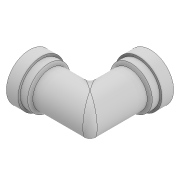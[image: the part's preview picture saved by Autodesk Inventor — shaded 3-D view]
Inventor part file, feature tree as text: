
AUTODESK INVENTOR PART (.ipt)
format: ipt  version: 2021 (Build 250183000, 183)  size: 292,864 bytes
history: native  units: mm
features: other x4, sketch x2, revolve x1, mirror x1, fillet x1
ambient origin geometry x8: Origin, YZ Plane, XZ Plane, XY Plane, X Axis, Y Axis, Z Axis, Center Point
bodies: Body1 (feature_tree)
feature tree (9):
  other  "Твердое тело1"
  revolve  "Вращение1"
  other  "РабПлоскость1"
  sketch  "Эскиз3"
  other  "РабПлоскость2"
  other  "Разделение1"
  mirror  "Зеркальное отражение1"
  fillet  "Сопряжение1"  Radius=16.0mm
  sketch  "Эскиз1"
